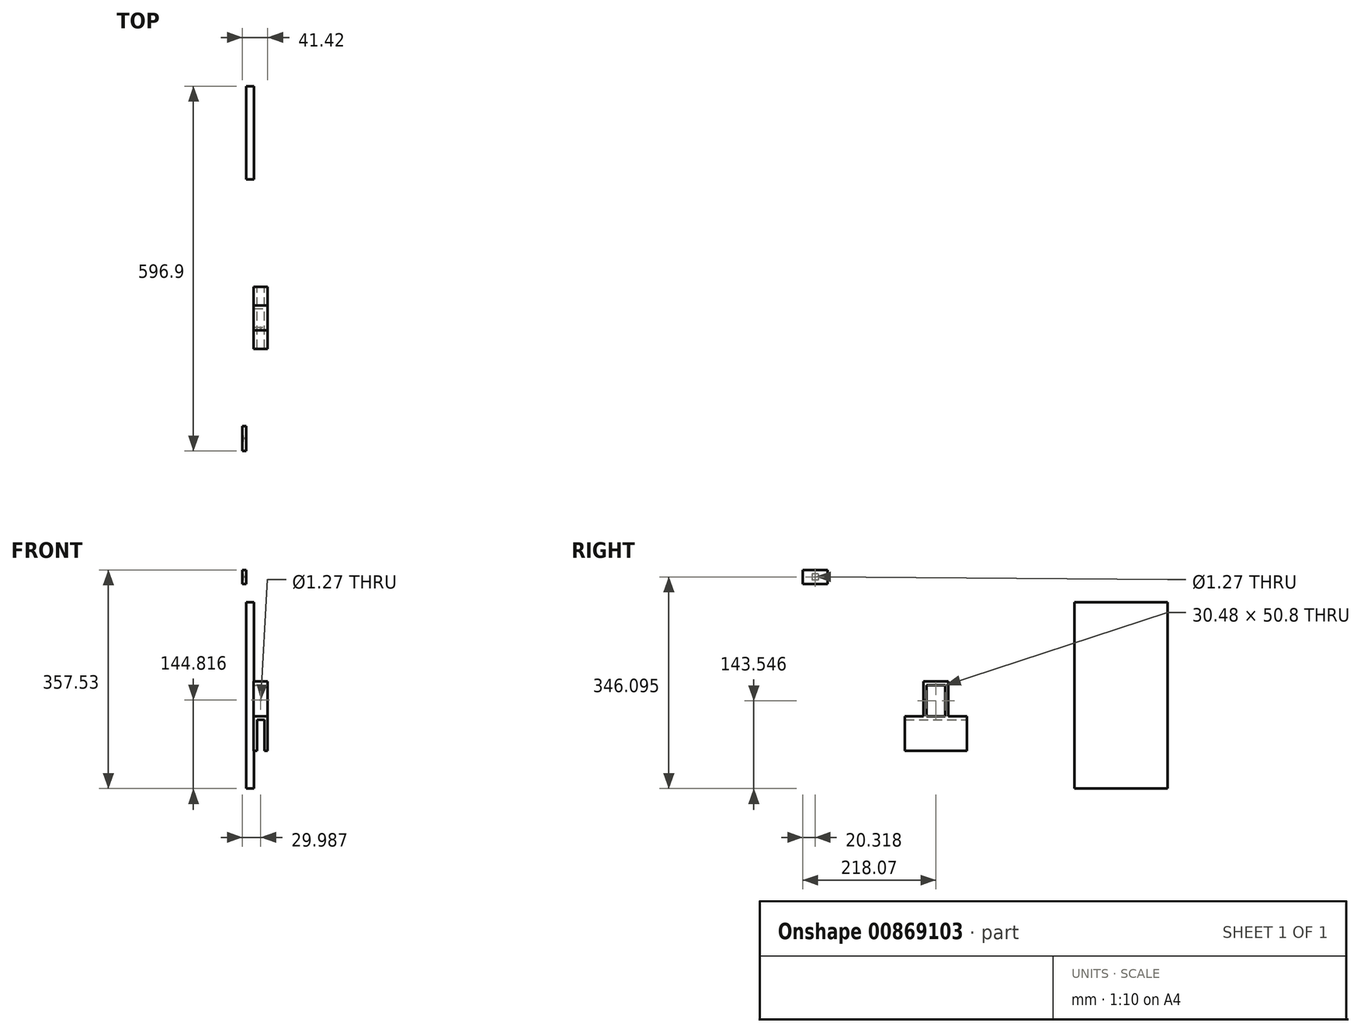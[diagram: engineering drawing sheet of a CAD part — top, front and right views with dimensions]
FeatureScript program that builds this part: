
annotation { "Feature Type Name" : "Feature", "Feature Type Description" : "" }
export const myFeature = defineFeature(function(context is Context, id is Id, definition is map)
    precondition{}
    {
        {
            var Q0;
            Q0=qCreatedBy(makeId("Front.planeOp"),FACE);
            var sketch = newSketch(context, id + "F0", { "sketchPlane" : qUnion([Q0])});
            skLineSegment(sketch, "E0", {"start": v(17.67, 4.24) * mm, "end": v(17.67, 55.04) * mm});
            skLineSegment(sketch, "E1", {"start": v(17.67, 55.04) * mm, "end": v(29.6, 55.04) * mm});
            skLineSegment(sketch, "E2", {"start": v(29.6, 55.04) * mm, "end": v(29.6, 4.24) * mm});
            skLineSegment(sketch, "E3.0", {"start": v(35.07, 60.5) * mm, "end": v(35.07, 4.24) * mm});
            skLineSegment(sketch, "E3.1", {"start": v(12.2, 60.5) * mm, "end": v(35.07, 60.5) * mm});
            skLineSegment(sketch, "E3.2", {"start": v(12.2, 4.24) * mm, "end": v(12.2, 60.5) * mm});
            skLineSegment(sketch, "E4", {"start": v(17.67, 4.24) * mm, "end": v(12.2, 4.24) * mm});
            skLineSegment(sketch, "E5", {"start": v(29.6, 4.24) * mm, "end": v(35.07, 4.24) * mm});
            skSolve(sketch);
        }
        {
            var Q0;
            Q0=makeQuery(id+"F0.imprint","IMPRINT",FACE,{"disambiguationData":[TD([[makeQuery(id+"F0.imprint","IMPRINT",EDGE,{"derivedFrom":sQuery(id+"F0.wireOp",EDGE,"E0")}),1.0]])]});
            extrude(context, id + "F1", {"entities" : qUnion([Q0]), "depth" : 101.6 * mm, "offsetDistance" : 25.4 * mm});
        }
        {
            var Q0;
            Q0=qCreatedBy(makeId("Right.planeOp"),FACE);
            var sketch = newSketch(context, id + "F2", { "sketchPlane" : qUnion([Q0])});
            skLineSegment(sketch, "E6.bottom", {"start": v(175.63, 247.15) * mm, "end": v(328.03, 247.15) * mm});
            skLineSegment(sketch, "E6.top", {"start": v(175.63, -57.65) * mm, "end": v(328.03, -57.65) * mm});
            skLineSegment(sketch, "E6.left", {"start": v(175.63, 247.15) * mm, "end": v(175.63, -57.65) * mm});
            skLineSegment(sketch, "E6.right", {"start": v(328.03, 247.15) * mm, "end": v(328.03, -57.65) * mm});
            skSolve(sketch);
        }
        {
            var Q0;
            Q0=makeQuery(id+"F2.imprint","IMPRINT",FACE,{"disambiguationData":[TD([[makeQuery(id+"F2.imprint","IMPRINT",EDGE,{"derivedFrom":sQuery(id+"F2.wireOp",EDGE,"E6.bottom")}),-1.0]])]});
            extrude(context, id + "F3", {"entities" : qUnion([Q0]), "depth" : 12.7 * mm, "offsetDistance" : 25.4 * mm});
        }
        {
            var Q0;
            Q0=makeQuery(id+"F1.opExtrude","SWEPT_FACE",FACE,{"disambiguationData":[OSD([sQuery(id+"F0.wireOp",EDGE,"E3.1")])]});
            var sketch = newSketch(context, id + "F4", { "sketchPlane" : qUnion([Q0])});
            skLineSegment(sketch, "E7.bottom", {"start": v(12.2, 0) * mm, "end": v(35.07, 0) * mm});
            skLineSegment(sketch, "E7.top", {"start": v(12.2, -5.08) * mm, "end": v(35.07, -5.08) * mm});
            skLineSegment(sketch, "E7.left", {"start": v(12.2, 0) * mm, "end": v(12.2, -5.08) * mm});
            skLineSegment(sketch, "E7.right", {"start": v(35.07, 0) * mm, "end": v(35.07, -5.08) * mm});
            skLineSegment(sketch, "E8.bottom", {"start": v(12.2, -30.48) * mm, "end": v(35.07, -30.48) * mm});
            skLineSegment(sketch, "E8.top", {"start": v(12.2, -35.56) * mm, "end": v(35.07, -35.56) * mm});
            skLineSegment(sketch, "E8.left", {"start": v(12.2, -30.48) * mm, "end": v(12.2, -35.56) * mm});
            skLineSegment(sketch, "E8.right", {"start": v(35.07, -30.48) * mm, "end": v(35.07, -35.56) * mm});
            skLineSegment(sketch, "E9", {"start": v(12.2, -50.8) * mm, "end": v(35.07, -50.8) * mm});
            skLineSegment(sketch, "E10.MirrorCS", {"start": v(12.2, -66.04) * mm, "end": v(35.07, -66.04) * mm});
            skLineSegment(sketch, "E11.MirrorCS", {"start": v(12.2, -71.12) * mm, "end": v(35.07, -71.12) * mm});
            skLineSegment(sketch, "E12.MirrorCS", {"start": v(12.2, -71.12) * mm, "end": v(12.2, -66.04) * mm});
            skLineSegment(sketch, "E13.MirrorCS", {"start": v(35.07, -71.12) * mm, "end": v(35.07, -66.04) * mm});
            skLineSegment(sketch, "E14.MirrorCS", {"start": v(12.2, -96.52) * mm, "end": v(35.07, -96.52) * mm});
            skLineSegment(sketch, "E15.MirrorCS", {"start": v(12.2, -101.6) * mm, "end": v(12.2, -96.52) * mm});
            skLineSegment(sketch, "E16.MirrorCS", {"start": v(12.2, -101.6) * mm, "end": v(35.07, -101.6) * mm});
            skLineSegment(sketch, "E17.MirrorCS", {"start": v(35.07, -101.6) * mm, "end": v(35.07, -96.52) * mm});
            skSolve(sketch);
        }
        {
            var Q0;
            Q0=makeQuery(id+"F4.imprint","IMPRINT",FACE,{"disambiguationData":[TD([[makeQuery(id+"F4.imprint","IMPRINT",EDGE,{"derivedFrom":sQuery(id+"F4.wireOp",EDGE,"E7.bottom")}),-1.0]])]});
            var Q1;
            Q1=makeQuery(id+"F4.imprint","IMPRINT",FACE,{"disambiguationData":[TD([[makeQuery(id+"F4.imprint","IMPRINT",EDGE,{"derivedFrom":sQuery(id+"F4.wireOp",EDGE,"E8.bottom")}),-1.0]])]});
            var Q2;
            Q2=makeQuery(id+"F4.imprint","IMPRINT",FACE,{"disambiguationData":[TD([[makeQuery(id+"F4.imprint","IMPRINT",EDGE,{"derivedFrom":sQuery(id+"F4.wireOp",EDGE,"E10.MirrorCS")}),-1.0]])]});
            var Q3;
            Q3=makeQuery(id+"F4.imprint","IMPRINT",FACE,{"disambiguationData":[TD([[makeQuery(id+"F4.imprint","IMPRINT",EDGE,{"derivedFrom":sQuery(id+"F4.wireOp",EDGE,"E14.MirrorCS")}),-1.0]])]});
            extrude(context, id + "F5", {"entities" : qUnion([Q0, Q1, Q2, Q3]), "operationType" : NewBodyOperationType.ADD, "depth" : 50.8 * mm, "offsetDistance" : 25.4 * mm});
        }
        {
            var Q0;
            Q0=makeQuery(id+"F5.opExtrude","CAP_FACE",FACE,{"disambiguationData":[OSD([sQuery(id+"F4.wireOp",EDGE,"E14.MirrorCS"),sQuery(id+"F4.wireOp",EDGE,"E15.MirrorCS"),sQuery(id+"F4.wireOp",EDGE,"E16.MirrorCS"),sQuery(id+"F4.wireOp",EDGE,"E17.MirrorCS")])],"isStart":false});
            var sketch = newSketch(context, id + "F6", { "sketchPlane" : qUnion([Q0])});
            skLineSegment(sketch, "E18.bottom", {"start": v(12.2, -101.6) * mm, "end": v(35.07, -101.6) * mm});
            skLineSegment(sketch, "E18.top", {"start": v(12.2, 0) * mm, "end": v(35.07, 0) * mm});
            skLineSegment(sketch, "E18.left", {"start": v(12.2, -101.6) * mm, "end": v(12.2, 0) * mm});
            skLineSegment(sketch, "E18.right", {"start": v(35.07, -101.6) * mm, "end": v(35.07, 0) * mm});
            skSolve(sketch);
        }
        {
            var Q0;
            {var subQ0=sQuery(id+"F6.wireOp",EDGE,"E18.bottom");Q0=makeQuery(id+"F6.imprint","IMPRINT",FACE,{"disambiguationData":[TD([[makeQuery(id+"F6.imprint","IMPRINT",EDGE,{"derivedFrom":subQ0}),1.0]])]});}
            var Q1;
            {var subQ0=sQuery(id+"F6.wireOp",EDGE,"E18.top");Q1=makeQuery(id+"F6.imprint","IMPRINT",FACE,{"disambiguationData":[TD([[makeQuery(id+"F6.imprint","IMPRINT",EDGE,{"derivedFrom":subQ0}),-1.0]])]});}
            extrude(context, id + "F7", {"entities" : qUnion([Q0, Q1]), "operationType" : NewBodyOperationType.ADD, "depth" : 6.35 * mm, "offsetDistance" : 25.4 * mm});
        }
        {
            var Q0;
            Q0=makeQuery(id+"F7.opExtrude","CAP_FACE",FACE,{"disambiguationData":[OSD([sQuery(id+"F6.wireOp",EDGE,"E18.bottom"),sQuery(id+"F6.wireOp",EDGE,"E18.top"),sQuery(id+"F6.wireOp",EDGE,"E18.left"),sQuery(id+"F6.wireOp",EDGE,"E18.right")])],"isStart":false});
            var sketch = newSketch(context, id + "F8", { "sketchPlane" : qUnion([Q0])});
            skCircle(sketch, "E19", {"center": v(23.64, -17.78) * mm, "radius": 1.27 * mm});
            skCircle(sketch, "E20", {"center": v(23.64, -83.82) * mm, "radius": 1.27 * mm});
            skSolve(sketch);
        }
        {
            var Q0;
            Q0=makeQuery(id+"F8.imprint","IMPRINT",FACE,{"disambiguationData":[TD([[makeQuery(id+"F8.imprint","IMPRINT",EDGE,{"derivedFrom":sQuery(id+"F8.wireOp",EDGE,"E20")}),1.0]])]});
            var Q1;
            Q1=makeQuery(id+"F8.imprint","IMPRINT",FACE,{"disambiguationData":[TD([[makeQuery(id+"F8.imprint","IMPRINT",EDGE,{"derivedFrom":sQuery(id+"F8.wireOp",EDGE,"E19")}),1.0]])]});
            extrude(context, id + "F9", {"entities" : qUnion([Q0, Q1]), "operationType" : NewBodyOperationType.REMOVE, "oppositeDirection" : true, "depth" : 7.62 * mm, "offsetDistance" : 25.4 * mm});
        }
        {
            var Q0;
            Q0=makeQuery(id+"F7.opExtrude","CAP_FACE",FACE,{"disambiguationData":[OSD([sQuery(id+"F6.wireOp",EDGE,"E18.bottom"),sQuery(id+"F6.wireOp",EDGE,"E18.top"),sQuery(id+"F6.wireOp",EDGE,"E18.left"),sQuery(id+"F6.wireOp",EDGE,"E18.right")])],"isStart":false});
            var sketch = newSketch(context, id + "F10", { "sketchPlane" : qUnion([Q0])});
            skLineSegment(sketch, "E21.bottom", {"start": v(12.2, -101.6) * mm, "end": v(35.07, -101.6) * mm});
            skLineSegment(sketch, "E21.top", {"start": v(12.2, -71.12) * mm, "end": v(35.07, -71.12) * mm});
            skLineSegment(sketch, "E21.left", {"start": v(12.2, -101.6) * mm, "end": v(12.2, -71.12) * mm});
            skLineSegment(sketch, "E21.right", {"start": v(35.07, -101.6) * mm, "end": v(35.07, -71.12) * mm});
            skLineSegment(sketch, "E22", {"start": v(35.07, -50.8) * mm, "end": v(12.2, -50.8) * mm});
            skLineSegment(sketch, "E23.MirrorCS", {"start": v(12.2, -30.48) * mm, "end": v(35.07, -30.48) * mm});
            skLineSegment(sketch, "E24.MirrorCS", {"start": v(12.2, 0) * mm, "end": v(12.2, -30.48) * mm});
            skLineSegment(sketch, "E25.MirrorCS", {"start": v(12.2, 0) * mm, "end": v(35.07, 0) * mm});
            skLineSegment(sketch, "E26.MirrorCS", {"start": v(35.07, 0) * mm, "end": v(35.07, -30.48) * mm});
            skSolve(sketch);
        }
        {
            var Q0;
            Q0=makeQuery(id+"F10.imprint","IMPRINT",FACE,{"disambiguationData":[TD([[makeQuery(id+"F10.imprint","IMPRINT",EDGE,{"derivedFrom":sQuery(id+"F10.wireOp",EDGE,"E21.bottom")}),1.0]])]});
            var Q1;
            Q1=makeQuery(id+"F10.imprint","IMPRINT",FACE,{"disambiguationData":[TD([[makeQuery(id+"F10.imprint","IMPRINT",EDGE,{"derivedFrom":sQuery(id+"F10.wireOp",EDGE,"E23.MirrorCS")}),1.0]])]});
            extrude(context, id + "F11", {"entities" : qUnion([Q0, Q1]), "operationType" : NewBodyOperationType.REMOVE, "oppositeDirection" : true, "depth" : 57.15 * mm, "offsetDistance" : 25.4 * mm});
        }
        {
            var Q0;
            Q0=makeQuery(id+"F11.boolean.opBoolean","MERGE",FACE,{"derivedFrom":[makeQuery(id+"F5.opExtrude","SWEPT_FACE",FACE,{"disambiguationData":[OSD([sQuery(id+"F4.wireOp",EDGE,"E11.MirrorCS")])]}),makeQuery(id+"F11.opExtrude","SWEPT_FACE",FACE,{"disambiguationData":[OSD([sQuery(id+"F10.wireOp",EDGE,"E21.top")])]})]});
            var sketch = newSketch(context, id + "F12", { "sketchPlane" : qUnion([Q0])});
            skCircle(sketch, "E27", {"center": v(23.64, 87.17) * mm, "radius": 0.64 * mm});
            skSolve(sketch);
        }
        {
            var Q0;
            Q0=makeQuery(id+"F12.imprint","IMPRINT",FACE,{"disambiguationData":[TD([[makeQuery(id+"F12.imprint","IMPRINT",EDGE,{"derivedFrom":sQuery(id+"F12.wireOp",EDGE,"E27")}),1.0]])]});
            extrude(context, id + "F13", {"entities" : qUnion([Q0]), "operationType" : NewBodyOperationType.REMOVE, "oppositeDirection" : true, "depth" : 25.4 * mm, "offsetDistance" : 25.4 * mm});
        }
        {
            var Q0;
            Q0=makeQuery(id+"F3.opExtrude","CAP_FACE",FACE,{"disambiguationData":[OSD([sQuery(id+"F2.wireOp",EDGE,"E6.bottom"),sQuery(id+"F2.wireOp",EDGE,"E6.top"),sQuery(id+"F2.wireOp",EDGE,"E6.left"),sQuery(id+"F2.wireOp",EDGE,"E6.right")])],"isStart":true});
            var sketch = newSketch(context, id + "F14", { "sketchPlane" : qUnion([Q0])});
            skLineSegment(sketch, "E28.bottom", {"start": v(228.23, 299.88) * mm, "end": v(268.87, 299.88) * mm});
            skLineSegment(sketch, "E28.top", {"start": v(228.23, 277.02) * mm, "end": v(268.87, 277.02) * mm});
            skLineSegment(sketch, "E28.left", {"start": v(228.23, 299.88) * mm, "end": v(228.23, 277.02) * mm});
            skLineSegment(sketch, "E28.right", {"start": v(268.87, 299.88) * mm, "end": v(268.87, 277.02) * mm});
            skSolve(sketch);
        }
        {
            var Q0;
            Q0=makeQuery(id+"F14.imprint","IMPRINT",FACE,{"disambiguationData":[TD([[makeQuery(id+"F14.imprint","IMPRINT",EDGE,{"derivedFrom":sQuery(id+"F14.wireOp",EDGE,"E28.bottom")}),-1.0]])]});
            extrude(context, id + "F15", {"entities" : qUnion([Q0]), "depth" : 6.35 * mm, "offsetDistance" : 25.4 * mm});
        }
        {
            var Q0;
            Q0=makeQuery(id+"F15.opExtrude","CAP_FACE",FACE,{"disambiguationData":[OSD([sQuery(id+"F14.wireOp",EDGE,"E28.bottom"),sQuery(id+"F14.wireOp",EDGE,"E28.top"),sQuery(id+"F14.wireOp",EDGE,"E28.left"),sQuery(id+"F14.wireOp",EDGE,"E28.right")])],"isStart":false});
            var sketch = newSketch(context, id + "F16", { "sketchPlane" : qUnion([Q0])});
            skCircle(sketch, "E29", {"center": v(248.55, 288.45) * mm, "radius": 0.64 * mm});
            skSolve(sketch);
        }
        {
            var Q0;
            Q0=makeQuery(id+"F16.imprint","IMPRINT",FACE,{"disambiguationData":[TD([[makeQuery(id+"F16.imprint","IMPRINT",EDGE,{"derivedFrom":sQuery(id+"F16.wireOp",EDGE,"E29")}),1.0]])]});
            extrude(context, id + "F17", {"entities" : qUnion([Q0]), "operationType" : NewBodyOperationType.REMOVE, "oppositeDirection" : true, "depth" : 25.4 * mm, "offsetDistance" : 25.4 * mm});
        }
        {
            var Q0;
            Q0=makeQuery(id+"F15.opExtrude","CAP_FACE",FACE,{"disambiguationData":[OSD([sQuery(id+"F14.wireOp",EDGE,"E28.bottom"),sQuery(id+"F14.wireOp",EDGE,"E28.top"),sQuery(id+"F14.wireOp",EDGE,"E28.left"),sQuery(id+"F14.wireOp",EDGE,"E28.right")])],"isStart":false});
            var sketch = newSketch(context, id + "F18", { "sketchPlane" : qUnion([Q0])});
            skLineSegment(sketch, "E30.bottom", {"start": v(243.47, 293.53) * mm, "end": v(253.63, 293.53) * mm});
            skLineSegment(sketch, "E30.top", {"start": v(243.47, 283.37) * mm, "end": v(253.63, 283.37) * mm});
            skLineSegment(sketch, "E30.left", {"start": v(243.47, 293.53) * mm, "end": v(243.47, 283.37) * mm});
            skLineSegment(sketch, "E30.right", {"start": v(253.63, 293.53) * mm, "end": v(253.63, 283.37) * mm});
            skPoint(sketch, "E30.middle", {"position": v(248.55, 288.45) * mm});
            skSolve(sketch);
        }
        {
            var Q0;
            Q0=makeQuery(id+"F18.imprint","IMPRINT",FACE,{"disambiguationData":[TD([[makeQuery(id+"F18.imprint","IMPRINT",EDGE,{"derivedFrom":sQuery(id+"F18.wireOp",EDGE,"E30.bottom")}),-1.0]])]});
            extrude(context, id + "F19", {"entities" : qUnion([Q0]), "operationType" : NewBodyOperationType.REMOVE, "oppositeDirection" : true, "depth" : 1.27 * mm, "offsetDistance" : 25.4 * mm});
        }
    });
